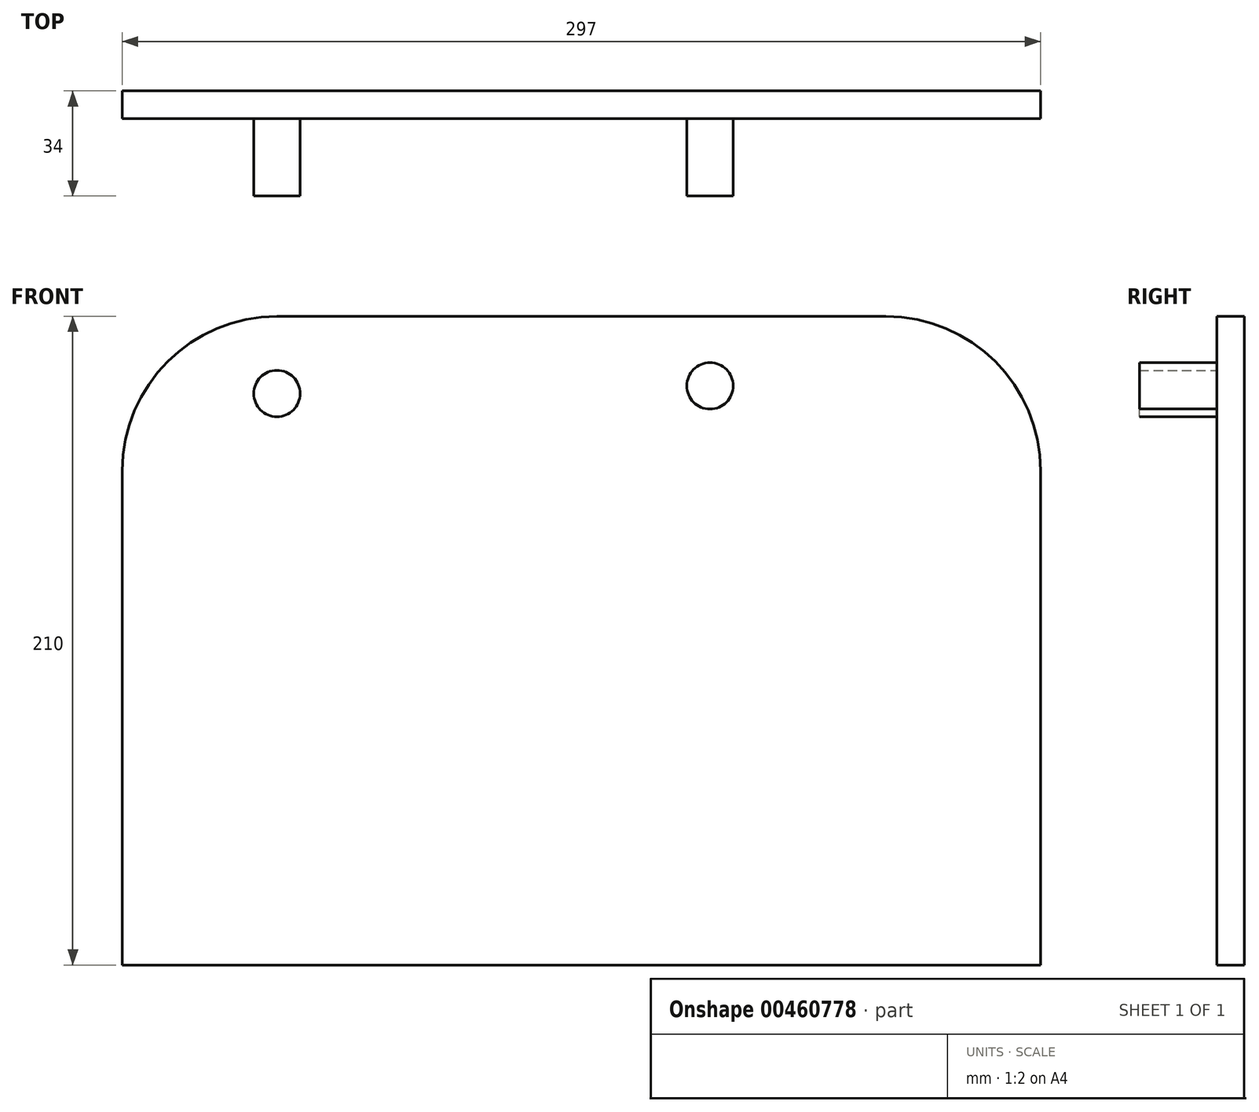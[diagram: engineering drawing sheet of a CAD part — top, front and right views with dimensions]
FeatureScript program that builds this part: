
annotation { "Feature Type Name" : "Feature", "Feature Type Description" : "" }
export const myFeature = defineFeature(function(context is Context, id is Id, definition is map)
    precondition{}
    {
        {
            var Q0;
            Q0=qCreatedBy(makeId("Front.planeOp"),FACE);
            var sketch = newSketch(context, id + "F0", { "sketchPlane" : qUnion([Q0])});
            skLineSegment(sketch, "E0.bottom", {"start": v(-141.16, 84.82) * mm, "end": v(55.84, 84.82) * mm});
            skLineSegment(sketch, "E0.top", {"start": v(-191.16, -125.18) * mm, "end": v(105.84, -125.18) * mm});
            skLineSegment(sketch, "E0.left", {"start": v(-191.16, 34.82) * mm, "end": v(-191.16, -125.18) * mm});
            skLineSegment(sketch, "E0.right", {"start": v(105.84, 34.82) * mm, "end": v(105.84, -125.18) * mm});
            skPoint(sketch, "E1.visualSharp", {"position": v(-191.16, 84.82) * mm});
            skArc(sketch, "E1.filletArc", {"start": v(-141.16, 84.82) * mm, "mid": v(-176.51, 70.18) * mm, "end": v(-191.16, 34.82) * mm});
            skPoint(sketch, "E2.visualSharp", {"position": v(105.84, 84.82) * mm});
            skArc(sketch, "E2.filletArc", {"start": v(105.84, 34.82) * mm, "mid": v(91.2, 70.18) * mm, "end": v(55.84, 84.82) * mm});
            skSolve(sketch);
        }
        {
            var Q0;
            Q0 = qSketchRegion(id + "F0", true);
            extrude(context, id + "F1", {"entities" : qUnion([Q0]), "depth" : 9 * mm});
        }
        {
            var Q0;
            Q0=makeQuery(id+"F1.opExtrude","CAP_FACE",FACE,{"disambiguationData":[OSD([sQuery(id+"F0.wireOp",EDGE,"E0.bottom"),sQuery(id+"F0.wireOp",EDGE,"E0.top"),sQuery(id+"F0.wireOp",EDGE,"E0.left"),sQuery(id+"F0.wireOp",EDGE,"E0.right"),sQuery(id+"F0.wireOp",EDGE,"E1.filletArc"),sQuery(id+"F0.wireOp",EDGE,"E2.filletArc")])],"isStart":false});
            var sketch = newSketch(context, id + "F2", { "sketchPlane" : qUnion([Q0])});
            skCircle(sketch, "E3", {"center": v(-141.16, 59.82) * mm, "radius": 7.5 * mm});
            skCircle(sketch, "E4", {"center": v(-1.07, 62.32) * mm, "radius": 7.5 * mm});
            skSolve(sketch);
        }
        {
            var Q0;
            Q0=makeQuery(id+"F2.imprint","IMPRINT",FACE,{"disambiguationData":[TD([[makeQuery(id+"F2.imprint","IMPRINT",EDGE,{"derivedFrom":sQuery(id+"F2.wireOp",EDGE,"E3")}),1.0]])]});
            var Q1;
            Q1=makeQuery(id+"F2.imprint","IMPRINT",FACE,{"disambiguationData":[TD([[makeQuery(id+"F2.imprint","IMPRINT",EDGE,{"derivedFrom":sQuery(id+"F2.wireOp",EDGE,"E4")}),1.0]])]});
            extrude(context, id + "F3", {"entities" : qUnion([Q0, Q1]), "operationType" : NewBodyOperationType.ADD, "depth" : 25 * mm});
        }
    });
